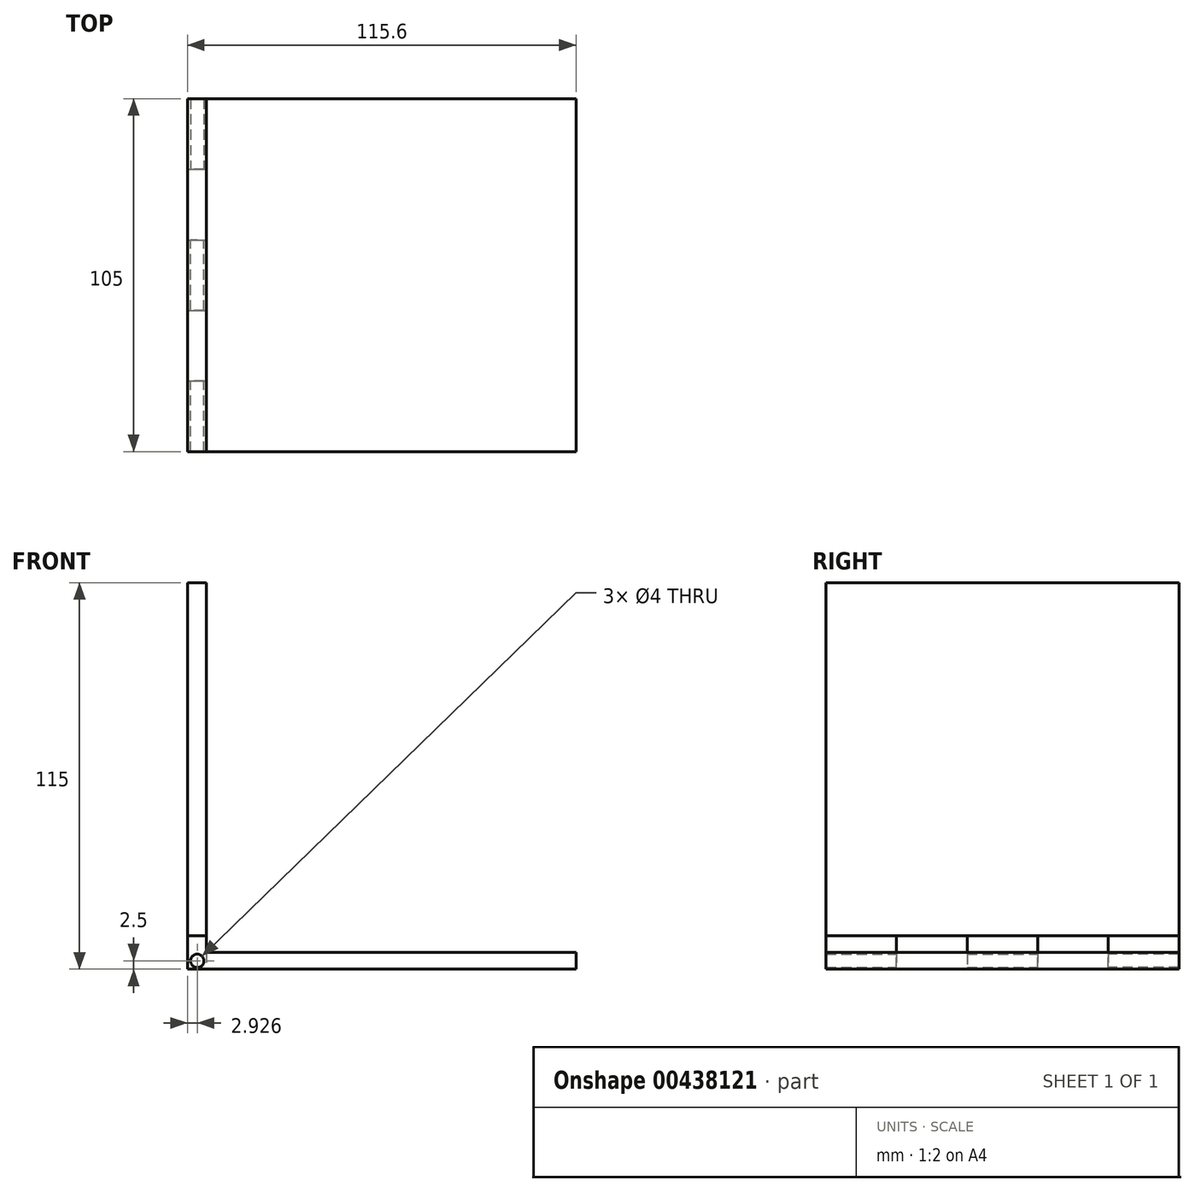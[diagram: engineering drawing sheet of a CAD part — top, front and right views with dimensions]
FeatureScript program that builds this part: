
annotation { "Feature Type Name" : "Feature", "Feature Type Description" : "" }
export const myFeature = defineFeature(function(context is Context, id is Id, definition is map)
    precondition{}
    {
        {
            var Q0;
            Q0=qCreatedBy(makeId("Top.planeOp"),FACE);
            var sketch = newSketch(context, id + "F0", { "sketchPlane" : qUnion([Q0])});
            skLineSegment(sketch, "E0.bottom", {"start": v(57.8, 52.5) * mm, "end": v(-57.8, 52.5) * mm});
            skLineSegment(sketch, "E0.top", {"start": v(57.8, -52.5) * mm, "end": v(-57.8, -52.5) * mm});
            skLineSegment(sketch, "E0.left", {"start": v(57.8, 52.5) * mm, "end": v(57.8, -52.5) * mm});
            skLineSegment(sketch, "E0.right", {"start": v(-57.8, 52.5) * mm, "end": v(-57.8, 31.5) * mm});
            skPoint(sketch, "E0.middle", {"position": v(0, 0) * mm});
            skPoint(sketch, "E1", {"position": v(-52.2, 52.5) * mm});
            skLineSegment(sketch, "E2", {"start": v(-57.8, 31.5) * mm, "end": v(-52.2, 31.5) * mm});
            skLineSegment(sketch, "E3", {"start": v(-52.2, 31.5) * mm, "end": v(-52.2, 10.5) * mm});
            skLineSegment(sketch, "E4", {"start": v(-52.2, 10.5) * mm, "end": v(-57.8, 10.5) * mm});
            skLineSegment(sketch, "E5", {"start": v(-57.8, 10.5) * mm, "end": v(-57.8, -10.5) * mm});
            skLineSegment(sketch, "E6", {"start": v(-57.8, -10.5) * mm, "end": v(-52.2, -10.5) * mm});
            skLineSegment(sketch, "E7", {"start": v(-52.2, -10.5) * mm, "end": v(-52.2, -31.5) * mm});
            skLineSegment(sketch, "E8", {"start": v(-52.2, -31.5) * mm, "end": v(-57.8, -31.5) * mm});
            skLineSegment(sketch, "E9.trimOffspring", {"start": v(-57.8, -31.5) * mm, "end": v(-57.8, -52.5) * mm});
            skLineSegment(sketch, "E10", {"start": v(-66.8, 0) * mm, "end": v(69.78, 0) * mm, "construction": true});
            skSolve(sketch);
        }
        {
            var Q0;
            Q0=makeQuery(id+"F0.imprint","IMPRINT",FACE,{"disambiguationData":[TD([[makeQuery(id+"F0.imprint","IMPRINT",EDGE,{"derivedFrom":sQuery(id+"F0.wireOp",EDGE,"E0.bottom")}),1.0]])]});
            extrude(context, id + "F1", {"entities" : qUnion([Q0]), "depth" : 5 * mm, "offsetDistance" : 25 * mm});
        }
        {
            var Q0;
            Q0=makeQuery(id+"F1.opExtrude","SWEPT_FACE",FACE,{"disambiguationData":[OSD([sQuery(id+"F0.wireOp",EDGE,"E2")])]});
            var sketch = newSketch(context, id + "F2", { "sketchPlane" : qUnion([Q0])});
            skCircle(sketch, "E11", {"center": v(-54.87, 2.5) * mm, "radius": 1.75 * mm});
            skPoint(sketch, "E11.centerSnap0", {"position": v(-57.8, 2.5) * mm});
            skSolve(sketch);
        }
        {
            var Q0;
            Q0=sQuery(id+"F2.wireOp",VERTEX,"E11.center");
            var Q1;
            Q1=makeQuery(id+"F1.opExtrude","SWEPT_BODY",BODY,{"disambiguationData":[OSD([sQuery(id+"F0.wireOp",EDGE,"E0.bottom"),sQuery(id+"F0.wireOp",EDGE,"E0.top"),sQuery(id+"F0.wireOp",EDGE,"E0.left"),sQuery(id+"F0.wireOp",EDGE,"E0.right"),sQuery(id+"F0.wireOp",EDGE,"E2"),sQuery(id+"F0.wireOp",EDGE,"E3"),sQuery(id+"F0.wireOp",EDGE,"E4"),sQuery(id+"F0.wireOp",EDGE,"E6"),sQuery(id+"F0.wireOp",EDGE,"E7"),sQuery(id+"F0.wireOp",EDGE,"E8"),sQuery(id+"F0.wireOp",EDGE,"E5"),sQuery(id+"F0.wireOp",EDGE,"E9.trimOffspring")])]});
            hole(context, id + "F3", {"style" : HoleStyle.SIMPLE, "endStyle" : HoleEndStyle.THROUGH, "oppositeDirection" : true, "holeDiameter" : 4 * mm, "majorDiameter" : 5 * mm, "isTappedThrough" : true, "tappedDepth" : 12 * mm, "tapClearance" : 3, "locations" : qUnion([Q0]), "scope" : qUnion([Q1])});
        }
        {
            var Q0;
            Q0=sQuery(id+"F2.wireOp",VERTEX,"E11.center");
            var Q1;
            Q1=makeQuery(id+"F1.opExtrude","SWEPT_BODY",BODY,{"disambiguationData":[OSD([sQuery(id+"F0.wireOp",EDGE,"E0.bottom"),sQuery(id+"F0.wireOp",EDGE,"E0.top"),sQuery(id+"F0.wireOp",EDGE,"E0.left"),sQuery(id+"F0.wireOp",EDGE,"E0.right"),sQuery(id+"F0.wireOp",EDGE,"E2"),sQuery(id+"F0.wireOp",EDGE,"E3"),sQuery(id+"F0.wireOp",EDGE,"E4"),sQuery(id+"F0.wireOp",EDGE,"E6"),sQuery(id+"F0.wireOp",EDGE,"E7"),sQuery(id+"F0.wireOp",EDGE,"E8"),sQuery(id+"F0.wireOp",EDGE,"E5"),sQuery(id+"F0.wireOp",EDGE,"E9.trimOffspring")])]});
            hole(context, id + "F4", {"style" : HoleStyle.SIMPLE, "endStyle" : HoleEndStyle.THROUGH, "holeDiameter" : 4 * mm, "majorDiameter" : 5 * mm, "isTappedThrough" : true, "tappedDepth" : 12 * mm, "tapClearance" : 3, "locations" : qUnion([Q0]), "scope" : qUnion([Q1])});
        }
        {
            var Q0;
            Q0=makeQuery(id+"F1.opExtrude","CAP_FACE",FACE,{"disambiguationData":[OSD([sQuery(id+"F0.wireOp",EDGE,"E0.bottom"),sQuery(id+"F0.wireOp",EDGE,"E0.top"),sQuery(id+"F0.wireOp",EDGE,"E0.left"),sQuery(id+"F0.wireOp",EDGE,"E0.right"),sQuery(id+"F0.wireOp",EDGE,"E2"),sQuery(id+"F0.wireOp",EDGE,"E3"),sQuery(id+"F0.wireOp",EDGE,"E4"),sQuery(id+"F0.wireOp",EDGE,"E6"),sQuery(id+"F0.wireOp",EDGE,"E7"),sQuery(id+"F0.wireOp",EDGE,"E8"),sQuery(id+"F0.wireOp",EDGE,"E5"),sQuery(id+"F0.wireOp",EDGE,"E9.trimOffspring")])],"isStart":false});
            var sketch = newSketch(context, id + "F5", { "sketchPlane" : qUnion([Q0])});
            skLineSegment(sketch, "E12", {"start": v(-52.2, 31.5) * mm, "end": v(-52.2, 52.5) * mm});
            skLineSegment(sketch, "E13", {"start": v(-52.2, 10.5) * mm, "end": v(-52.2, -10.5) * mm});
            skLineSegment(sketch, "E14", {"start": v(-52.2, -31.5) * mm, "end": v(-52.2, -52.5) * mm});
            skSolve(sketch);
        }
        {
            var Q0;
            {var subQ0=sQuery(id+"F5.wireOp",EDGE,"E12");Q0=makeQuery(id+"F5.imprint","IMPRINT",FACE,{"disambiguationData":[TD([[makeQuery(id+"F5.imprint","IMPRINT",EDGE,{"derivedFrom":subQ0}),1.0]])]});}
            var Q1;
            Q1=makeQuery(id+"F5.imprint","IMPRINT",FACE,{"disambiguationData":[TD([[makeQuery(id+"F5.imprint","IMPRINT",EDGE,{"derivedFrom":sQuery(id+"F5.wireOp",EDGE,"E13")}),-1.0]])]});
            var Q2;
            {var subQ0=sQuery(id+"F5.wireOp",EDGE,"E14");Q2=makeQuery(id+"F5.imprint","IMPRINT",FACE,{"disambiguationData":[TD([[makeQuery(id+"F5.imprint","IMPRINT",EDGE,{"derivedFrom":subQ0}),-1.0]])]});}
            extrude(context, id + "F6", {"entities" : qUnion([Q0, Q1, Q2]), "operationType" : NewBodyOperationType.ADD, "depth" : 5 * mm, "offsetDistance" : 25 * mm});
        }
        {
            var Q0;
            Q0=makeQuery(id+"F1.opExtrude","SWEPT_FACE",FACE,{"disambiguationData":[OSD([sQuery(id+"F0.wireOp",EDGE,"E3")])]});
            var sketch = newSketch(context, id + "F7", { "sketchPlane" : qUnion([Q0])});
            skLineSegment(sketch, "E15.0", {"start": v(-31.5, 10) * mm, "end": v(-31.5, 0) * mm});
            skLineSegment(sketch, "E16.0", {"start": v(-10.5, 10) * mm, "end": v(-10.5, 0) * mm});
            skLineSegment(sketch, "E17.0", {"start": v(10.5, 10) * mm, "end": v(10.5, 0) * mm});
            skLineSegment(sketch, "E18.0", {"start": v(31.5, 10) * mm, "end": v(31.5, 0) * mm});
            skLineSegment(sketch, "E19.bottom", {"start": v(-31.5, 10) * mm, "end": v(-10.5, 10) * mm});
            skLineSegment(sketch, "E19.top", {"start": v(-31.5, -0.8) * mm, "end": v(-10.5, -0.8) * mm});
            skLineSegment(sketch, "E19.left", {"start": v(-31.5, 10) * mm, "end": v(-31.5, -0.8) * mm});
            skLineSegment(sketch, "E19.right", {"start": v(-10.5, 10) * mm, "end": v(-10.5, -0.8) * mm});
            skLineSegment(sketch, "E20.bottom", {"start": v(10.5, 10) * mm, "end": v(31.5, 10) * mm});
            skLineSegment(sketch, "E20.top", {"start": v(10.5, 0) * mm, "end": v(31.5, 0) * mm});
            skSolve(sketch);
        }
        {
            var Q0;
            {var subQ0=sQuery(id+"F7.wireOp",EDGE,"E19.bottom");Q0=makeQuery(id+"F7.imprint","IMPRINT",FACE,{"disambiguationData":[TD([[makeQuery(id+"F7.imprint","IMPRINT",EDGE,{"derivedFrom":subQ0}),-1.0]])]});}
            var Q1;
            {var subQ1=sQuery(id+"F0.wireOp",EDGE,"E3");var subQ2=makeQuery(id+"F1.opExtrude","CAP_EDGE",EDGE,{"disambiguationData":[OSD([subQ1])],"isStart":true});Q1=makeQuery(id+"F7.imprint","IMPRINT",FACE,{"disambiguationData":[TD([[makeQuery(id+"F7.imprint","IMPRINT",EDGE,{"derivedFrom":subQ2}),1.0]])]});}
            var Q2;
            Q2=makeQuery(id+"F7.imprint","IMPRINT",FACE,{"disambiguationData":[TD([[makeQuery(id+"F7.imprint","IMPRINT",EDGE,{"derivedFrom":sQuery(id+"F7.wireOp",EDGE,"E20.bottom")}),-1.0]])]});
            extrude(context, id + "F8", {"entities" : qUnion([Q0, Q1, Q2]), "depth" : 5.6 * mm, "offsetDistance" : 25 * mm});
        }
        {
            var Q0;
            Q0=makeQuery(id+"F6.opExtrude","CAP_FACE",FACE,{"disambiguationData":[OSD([sQuery(id+"F0.wireOp",EDGE,"E0.bottom"),sQuery(id+"F0.wireOp",EDGE,"E0.right"),sQuery(id+"F0.wireOp",EDGE,"E2"),sQuery(id+"F5.wireOp",EDGE,"E12")])],"isStart":false});
            var sketch = newSketch(context, id + "F9", { "sketchPlane" : qUnion([Q0])});
            skLineSegment(sketch, "E21.0", {"start": v(-57.8, -31.5) * mm, "end": v(-57.8, -52.5) * mm});
            skLineSegment(sketch, "E22.0", {"start": v(-52.2, -52.5) * mm, "end": v(-57.8, -52.5) * mm});
            skLineSegment(sketch, "E23.bottom", {"start": v(-52.2, 52.5) * mm, "end": v(-57.8, 52.5) * mm});
            skLineSegment(sketch, "E23.left", {"start": v(-52.2, 52.5) * mm, "end": v(-52.2, -52.5) * mm});
            skLineSegment(sketch, "E23.right", {"start": v(-57.8, 52.5) * mm, "end": v(-57.8, -52.5) * mm});
            skSolve(sketch);
        }
        {
            var Q0;
            {var subQ0=sQuery(id+"F9.wireOp",EDGE,"E23.bottom");Q0=makeQuery(id+"F9.imprint","IMPRINT",FACE,{"disambiguationData":[TD([[makeQuery(id+"F9.imprint","IMPRINT",EDGE,{"derivedFrom":subQ0}),1.0]])]});}
            var Q1;
            {var subQ0=sQuery(id+"F9.wireOp",EDGE,"E22.0");Q1=makeQuery(id+"F9.imprint","IMPRINT",FACE,{"disambiguationData":[TD([[makeQuery(id+"F9.imprint","IMPRINT",EDGE,{"derivedFrom":subQ0}),-1.0]])]});}
            extrude(context, id + "F10", {"entities" : qUnion([Q0, Q1]), "depth" : 105 * mm, "offsetDistance" : 25 * mm});
        }
    });
